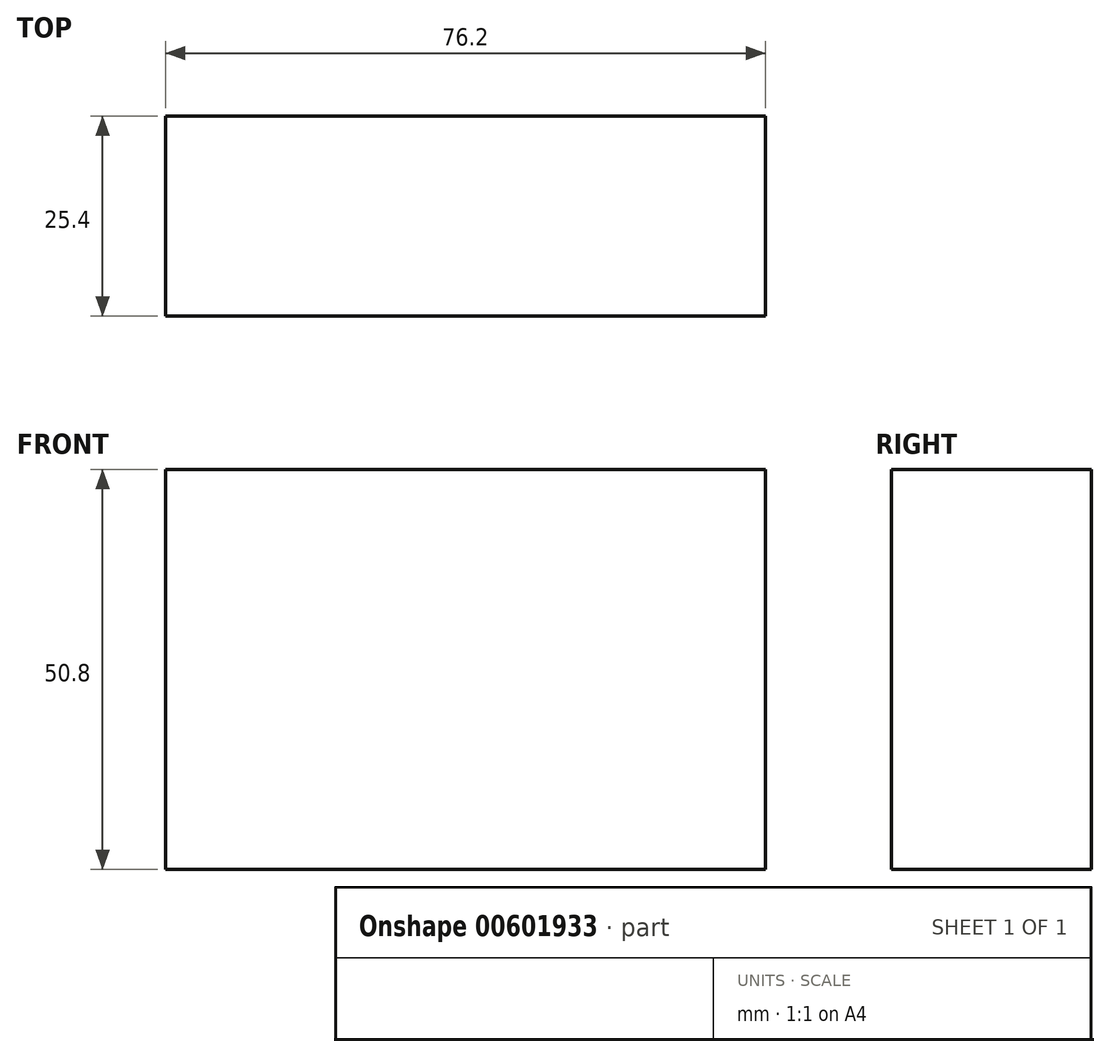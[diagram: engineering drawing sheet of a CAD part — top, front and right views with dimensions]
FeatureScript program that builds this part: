
annotation { "Feature Type Name" : "Feature", "Feature Type Description" : "" }
export const myFeature = defineFeature(function(context is Context, id is Id, definition is map)
    precondition{}
    {
        {
            var Q0;
            Q0=qCreatedBy(makeId("Front.planeOp"),FACE);
            var sketch = newSketch(context, id + "F0", { "sketchPlane" : qUnion([Q0])});
            skLineSegment(sketch, "E0", {"start": v(-31.5, 45.82) * mm, "end": v(44.7, 45.82) * mm});
            skLineSegment(sketch, "E1", {"start": v(-31.5, 45.82) * mm, "end": v(-31.5, -4.98) * mm});
            skLineSegment(sketch, "E2", {"start": v(44.7, 45.82) * mm, "end": v(44.7, -4.98) * mm});
            skLineSegment(sketch, "E3", {"start": v(-31.5, -4.98) * mm, "end": v(44.7, -4.98) * mm});
            skSolve(sketch);
        }
        {
            var Q0;
            Q0 = qSketchRegion(id + "F0", true);
            extrude(context, id + "F1", {"entities" : qUnion([Q0]), "depth" : 25.4 * mm, "offsetDistance" : 25.4 * mm});
        }
        {
            var Q0;
            Q0 = qSketchRegion(id + "F0", true);
            extrude(context, id + "F2", {"entities" : qUnion([Q0]), "operationType" : NewBodyOperationType.ADD, "depth" : 25.4 * mm, "offsetDistance" : 25.4 * mm});
        }
        {
            var Q0;
            Q0 = qSketchRegion(id + "F0", true);
            extrude(context, id + "F3", {"entities" : qUnion([Q0]), "operationType" : NewBodyOperationType.ADD, "depth" : 25.4 * mm, "offsetDistance" : 25.4 * mm});
        }
    });
